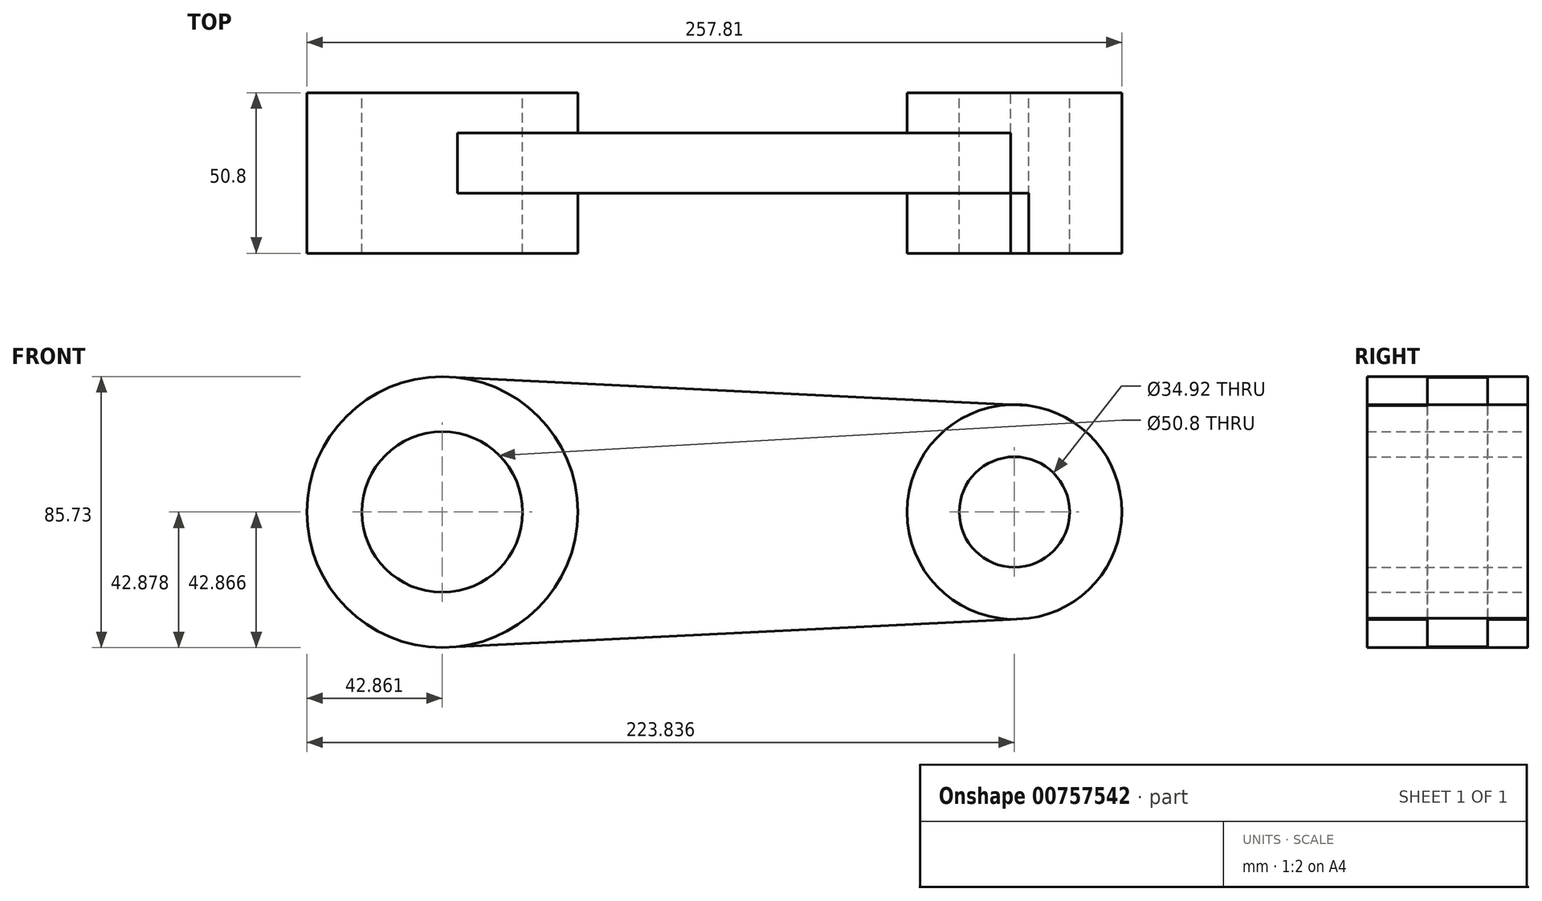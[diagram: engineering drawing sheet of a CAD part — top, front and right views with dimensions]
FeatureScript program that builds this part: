
annotation { "Feature Type Name" : "Feature", "Feature Type Description" : "" }
export const myFeature = defineFeature(function(context is Context, id is Id, definition is map)
    precondition{}
    {
        {
            var Q0;
            Q0=qCreatedBy(makeId("Front.planeOp"),FACE);
            var sketch = newSketch(context, id + "F0", { "sketchPlane" : qUnion([Q0])});
            skCircle(sketch, "E0", {"center": v(-47.66, 38.67) * mm, "radius": 25.4 * mm});
            skCircle(sketch, "E1", {"center": v(-47.66, 38.67) * mm, "radius": 42.86 * mm});
            skCircle(sketch, "E2", {"center": v(133.32, 38.68) * mm, "radius": 17.46 * mm});
            skCircle(sketch, "E3", {"center": v(133.32, 38.68) * mm, "radius": 33.97 * mm});
            skLineSegment(sketch, "E4", {"start": v(-42.83, 81.26) * mm, "end": v(137.9, 72.34) * mm});
            skLineSegment(sketch, "E5", {"start": v(137.9, 5.02) * mm, "end": v(-42.83, -3.92) * mm});
            skSolve(sketch);
        }
        {
            var Q0;
            {var subQ0=sQuery(id+"F0.wireOp",EDGE,"E4");var subQ1=sQuery(id+"F0.wireOp",EDGE,"E3");var subQ2=makeQuery(id+"F0.imprint","INTERSECT",VERTEX,{"disambiguationData":[OD(0.0)],"derivedFrom":[subQ1,subQ0]});Q0=makeQuery(id+"F0.imprint","IMPRINT",FACE,{"disambiguationData":[TD([[makeQuery(id+"F0.imprint","IMPRINT",EDGE,{"disambiguationData":[TD([[subQ2,-1.0]])],"derivedFrom":subQ1}),1.0]])]});}
            var Q1;
            {var subQ0=sQuery(id+"F0.wireOp",EDGE,"E5");var subQ1=sQuery(id+"F0.wireOp",EDGE,"E3");var subQ2=makeQuery(id+"F0.imprint","INTERSECT",VERTEX,{"disambiguationData":[OD(0.0)],"derivedFrom":[subQ1,subQ0]});Q1=makeQuery(id+"F0.imprint","IMPRINT",FACE,{"disambiguationData":[TD([[makeQuery(id+"F0.imprint","IMPRINT",EDGE,{"disambiguationData":[TD([[subQ2,1.0]])],"derivedFrom":subQ1}),1.0]])]});}
            var Q2;
            Q2=makeQuery(id+"F0.imprint","IMPRINT",FACE,{"disambiguationData":[TD([[makeQuery(id+"F0.imprint","IMPRINT",EDGE,{"derivedFrom":sQuery(id+"F0.wireOp",EDGE,"E2")}),-1.0]])]});
            extrude(context, id + "F1", {"entities" : qUnion([Q0, Q1, Q2]), "depth" : 31.75 * mm, "offsetDistance" : 25.4 * mm});
        }
        {
            var Q0;
            {var subQ0=sQuery(id+"F0.wireOp",EDGE,"E4");var subQ1=sQuery(id+"F0.wireOp",EDGE,"E1");var subQ2=makeQuery(id+"F0.imprint","INTERSECT",VERTEX,{"derivedFrom":[subQ1,subQ0]});Q0=makeQuery(id+"F0.imprint","IMPRINT",FACE,{"disambiguationData":[TD([[makeQuery(id+"F0.imprint","IMPRINT",EDGE,{"disambiguationData":[TD([[subQ2,1.0]])],"derivedFrom":subQ1}),-1.0]])]});}
            extrude(context, id + "F2", {"entities" : qUnion([Q0]), "operationType" : NewBodyOperationType.ADD, "depth" : 31.75 * mm, "offsetDistance" : 25.4 * mm});
        }
        {
            var Q0;
            Q0=makeQuery(id+"F0.imprint","IMPRINT",FACE,{"disambiguationData":[TD([[makeQuery(id+"F0.imprint","IMPRINT",EDGE,{"derivedFrom":sQuery(id+"F0.wireOp",EDGE,"E0")}),-1.0]])]});
            extrude(context, id + "F3", {"entities" : qUnion([Q0]), "operationType" : NewBodyOperationType.ADD, "depth" : 50.8 * mm, "offsetDistance" : 25.4 * mm});
        }
        {
            var Q0;
            {var subQ0=sQuery(id+"F0.wireOp",EDGE,"E4");var subQ1=sQuery(id+"F0.wireOp",EDGE,"E1");var subQ2=makeQuery(id+"F0.imprint","INTERSECT",VERTEX,{"derivedFrom":[subQ1,subQ0]});Q0=makeQuery(id+"F0.imprint","IMPRINT",FACE,{"disambiguationData":[TD([[makeQuery(id+"F0.imprint","IMPRINT",EDGE,{"disambiguationData":[TD([[subQ2,1.0]])],"derivedFrom":subQ1}),-1.0]])]});}
            extrude(context, id + "F4", {"entities" : qUnion([Q0]), "operationType" : NewBodyOperationType.REMOVE, "depth" : 12.7 * mm, "offsetDistance" : 25.4 * mm});
        }
        {
            var Q0;
            Q0=makeQuery(id+"F0.imprint","IMPRINT",FACE,{"disambiguationData":[TD([[makeQuery(id+"F0.imprint","IMPRINT",EDGE,{"derivedFrom":sQuery(id+"F0.wireOp",EDGE,"E2")}),-1.0]])]});
            extrude(context, id + "F5", {"entities" : qUnion([Q0]), "operationType" : NewBodyOperationType.ADD, "depth" : 50.8 * mm, "offsetDistance" : 25.4 * mm});
        }
    });
